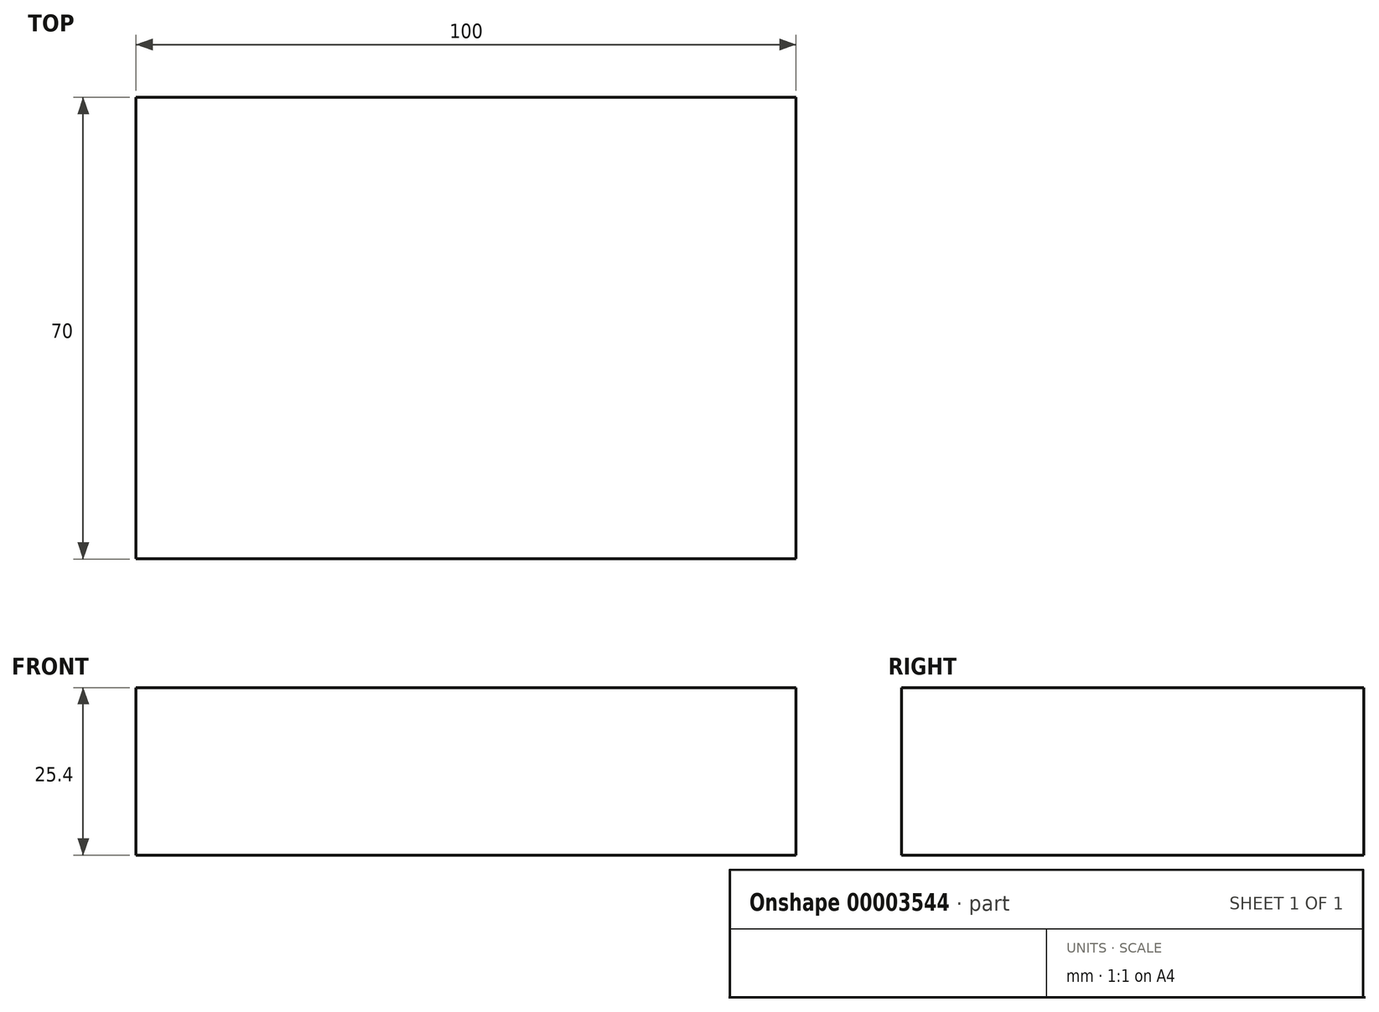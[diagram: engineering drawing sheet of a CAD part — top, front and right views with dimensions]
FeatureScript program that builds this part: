
annotation { "Feature Type Name" : "Feature", "Feature Type Description" : "" }
export const myFeature = defineFeature(function(context is Context, id is Id, definition is map)
    precondition{}
    {
        {
            var Q0;
            Q0=qCreatedBy(makeId("Top.planeOp"),FACE);
            var sketch = newSketch(context, id + "F0", { "sketchPlane" : qUnion([Q0])});
            skLineSegment(sketch, "E0", {"start": v(-42.86, 30.2) * mm, "end": v(57.14, 30.2) * mm});
            skLineSegment(sketch, "E1", {"start": v(57.14, 30.2) * mm, "end": v(57.14, -39.8) * mm});
            skLineSegment(sketch, "E2", {"start": v(57.14, -39.8) * mm, "end": v(-42.86, -39.8) * mm});
            skLineSegment(sketch, "E3", {"start": v(-42.86, -39.8) * mm, "end": v(-42.86, 30.2) * mm});
            skSolve(sketch);
        }
        {
            var Q0;
            Q0 = qSketchRegion(id + "F0", true);
            extrude(context, id + "F1", {"entities" : qUnion([Q0]), "depth" : 25.4 * mm});
        }
    });
